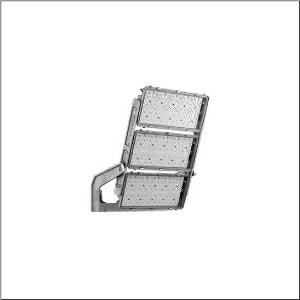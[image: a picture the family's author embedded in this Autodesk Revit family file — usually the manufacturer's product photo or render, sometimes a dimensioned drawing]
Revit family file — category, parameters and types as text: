
# Revit family: floodlight_fl_11_maxi_pro_remote___pl33tblc_5xa779425h01aa_685d
name_source: partatom
category: Lighting Fixtures
units: mm (PartAtom-declared; Revit-internal decimal feet)

## family parameters
Cut with Voids When Loaded = No
Host = Face
Light Source = No
Part Type = Normal
Room Calculation Point = No
Round Connector Dimension = Use Diameter
Shared = No

## types (1)
- --- (1 x LED, 117060 lm, 1335.4 W, 3000K)
    Apparent Load = 1335 VA
    CIE Flux Codes = 24 77 100 100 100
    Color Rendering = 70
    Color Temperature = 3000K
    Default Elevation = 1800 mm
    Description = Floodlight FL 11  maxi  pro Remote floodlight; light control with lens of PMMA; cover panel of toughened safety glass, transparent; light distribution: PL33TBLC, asymmetric direct distribution, LEDcolour temperature: 3000K, rated luminous flux: 117.060lm, colour rendering: CRI > 70, light colour: 730; luminous efficacy: 88lm/W; brightness control: DALI 2 (1 DALI address); with terminal, 8-pole, max. 2.5mm², mains connection: 220..240V/380..400V AC, 50/60Hz, surge voltage resistance: line to ground: 10kV, ECG replaceable separately, LED unit replaceable without ESD environment, dustproof LED module, dimming range 10..100%, no afterglow with DALI off / DMX off command; 1335W floodlight with 2x LED unit of diecast aluminium, coated grey; length: 713mm / width: 651mm / height: 338mm; mounting bracket, of diecast aluminium, uncoated, natural, equipment: Power, protection rating (complete): IP66; insulation class (complete): insulation class I (protective earthing); certification: CE, ENEC, VDE; ball protection: ball impact resistance with accessories, impact resistance: IK07; rated ambient temperature 10°C, only for outdoor installations, permissible operating ambient temperature: -40..+30°C, permissible storage temperature: -40..+85°Cpackaging unit: 1 piece

Light Distribution: PL33TBLC
    Height = 320 mm
    Lamp = 1 x LED
    Lamp Light Flux = 117060 lm
    Lamp Power = 1335.4 W
    Lamp count = 1
    Length = 1002 mm
    Luminous efficacy = 88 lm/W
    Manufacturer = Siteco
    ModVariant = No
    Model = 5XA779425H01AA
    Mounting Place = Ceiling
    Mounting Type = Surface mounted
    Number of Poles = 1
    OnlyDefault = Yes
    Power Factor = 1
    Product Name = Floodlight FL 11 maxi pro Remote | PL33TBLC
    Product group = floodlight | ceiling mounted
    ProductGroupID = 301
    Protection Class = Protection class I
    Protection Degree = IP 66
    RLX_Detail_Level = 1
    RLX_Emergency_Light_Flux = 0 lm
    RLX_Emergency_Type = 0
    RLX_Emergency_Type_DB = No
    RlxData = <blob elided: 52185 chars, md5=0f8cd0b8>
    Socket = socket
    Standby Power = 0 W
    System Light Flux = 117060 lm
    System Power = 1335 W
    Type Comments = factory setting: luminous flux: 100 % | dim-lin: 254 | 920 mA
    Type Image = l_1349141.jpg
    URL = http://relux.com
    VarID = @adj_096050
    Voltage = 0 V
    Weight = 0.00 kg
    Width = 655 mm

## geometry (parser evidence)
native form markers: Blend x4, Sweep x15
no freeform markers — native parametric forms only
